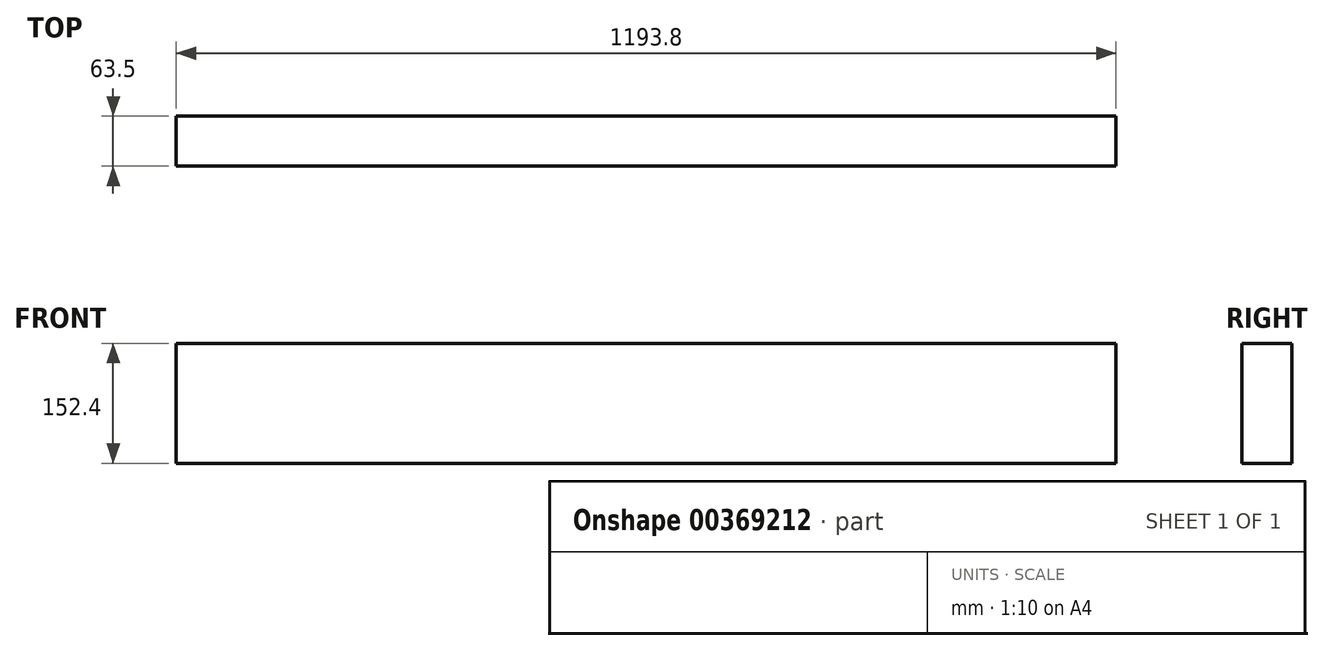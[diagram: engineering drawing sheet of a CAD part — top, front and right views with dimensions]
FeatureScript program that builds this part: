
annotation { "Feature Type Name" : "Feature", "Feature Type Description" : "" }
export const myFeature = defineFeature(function(context is Context, id is Id, definition is map)
    precondition{}
    {
        {
            var Q0;
            Q0=qCreatedBy(makeId("Front.planeOp"),FACE);
            var sketch = newSketch(context, id + "F0", { "sketchPlane" : qUnion([Q0])});
            skLineSegment(sketch, "E0.bottom", {"start": v(-1193.8, -480.54) * mm, "end": v(0, -480.54) * mm});
            skLineSegment(sketch, "E0.top", {"start": v(-1193.8, -632.94) * mm, "end": v(0, -632.94) * mm});
            skLineSegment(sketch, "E0.left", {"start": v(-1193.8, -480.54) * mm, "end": v(-1193.8, -632.94) * mm});
            skLineSegment(sketch, "E0.right", {"start": v(0, -480.54) * mm, "end": v(0, -632.94) * mm});
            skSolve(sketch);
        }
        {
            var Q0;
            Q0=makeQuery(id+"F0.imprint","IMPRINT",FACE,{"disambiguationData":[TD([[makeQuery(id+"F0.imprint","IMPRINT",EDGE,{"derivedFrom":sQuery(id+"F0.wireOp",EDGE,"E0.bottom")}),-1.0]])]});
            extrude(context, id + "F1", {"entities" : qUnion([Q0]), "depth" : 63.5 * mm});
        }
    });
